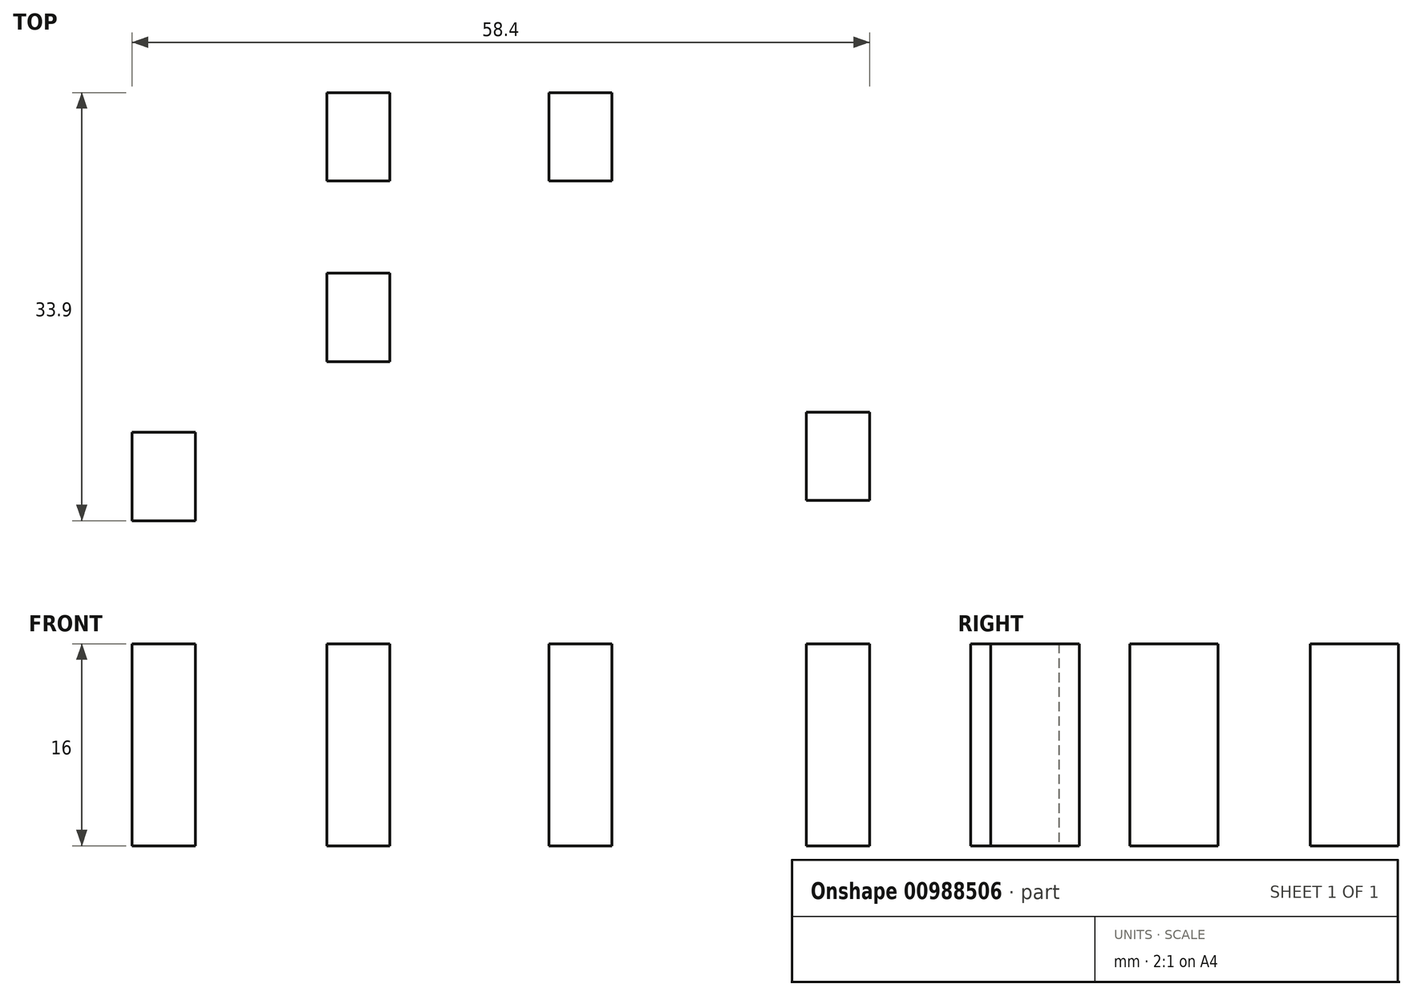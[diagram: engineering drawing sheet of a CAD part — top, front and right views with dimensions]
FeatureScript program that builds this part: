
annotation { "Feature Type Name" : "Feature", "Feature Type Description" : "" }
export const myFeature = defineFeature(function(context is Context, id is Id, definition is map)
    precondition{}
    {
        {
            var Q0;
            Q0=qCreatedBy(makeId("Top.planeOp"),FACE);
            var sketch = newSketch(context, id + "F0", { "sketchPlane" : qUnion([Q0])});
            skLineSegment(sketch, "E0.bottom", {"start": v(-19.73, 14.99) * mm, "end": v(-14.73, 14.99) * mm});
            skLineSegment(sketch, "E0.top", {"start": v(-19.73, 7.99) * mm, "end": v(-14.73, 7.99) * mm});
            skLineSegment(sketch, "E0.left", {"start": v(-19.73, 14.99) * mm, "end": v(-19.73, 7.99) * mm});
            skLineSegment(sketch, "E0.right", {"start": v(-14.73, 14.99) * mm, "end": v(-14.73, 7.99) * mm});
            skSolve(sketch);
        }
        {
            var Q0;
            Q0=makeQuery(id+"F0.imprint","IMPRINT",FACE,{"disambiguationData":[TD([[makeQuery(id+"F0.imprint","IMPRINT",EDGE,{"derivedFrom":sQuery(id+"F0.wireOp",EDGE,"E0.bottom")}),-1.0]])]});
            extrude(context, id + "F1", {"entities" : qUnion([Q0]), "endBound" : BoundingType.SYMMETRIC, "depth" : 16 * mm, "offsetDistance" : 25 * mm});
        }
        {
            var Q0;
            Q0=makeQuery(id+"F1.opExtrude","SWEPT_BODY",BODY,{"disambiguationData":[OSD([sQuery(id+"F0.wireOp",EDGE,"E0.bottom"),sQuery(id+"F0.wireOp",EDGE,"E0.top"),sQuery(id+"F0.wireOp",EDGE,"E0.left"),sQuery(id+"F0.wireOp",EDGE,"E0.right")])]});
            transform(context, id + "F2", {"entities" : qUnion([Q0]), "transformType" : TransformType.TRANSLATION_3D, "dx" : 17.6 * mm, "dy" : 0 * mm, "dz" : 0 * mm, "makeCopy" : true});
        }
        {
            var Q0;
            Q0=makeQuery(id+"F2.opPattern","COPY",BODY,{"derivedFrom":makeQuery(id+"F1.opExtrude","SWEPT_BODY",BODY,{"disambiguationData":[OSD([sQuery(id+"F0.wireOp",EDGE,"E0.bottom"),sQuery(id+"F0.wireOp",EDGE,"E0.top"),sQuery(id+"F0.wireOp",EDGE,"E0.left"),sQuery(id+"F0.wireOp",EDGE,"E0.right")])]}),"instanceName":"1"});
            transform(context, id + "F3", {"entities" : qUnion([Q0]), "transformType" : TransformType.TRANSLATION_3D, "dx" : 20.4 * mm, "dy" : -25.3 * mm, "dz" : 0 * mm, "makeCopy" : true});
        }
        {
            var Q0;
            Q0=makeQuery(id+"F1.opExtrude","SWEPT_BODY",BODY,{"disambiguationData":[OSD([sQuery(id+"F0.wireOp",EDGE,"E0.bottom"),sQuery(id+"F0.wireOp",EDGE,"E0.top"),sQuery(id+"F0.wireOp",EDGE,"E0.left"),sQuery(id+"F0.wireOp",EDGE,"E0.right")])]});
            transform(context, id + "F4", {"entities" : qUnion([Q0]), "transformType" : TransformType.TRANSLATION_3D, "dx" : -15.4 * mm, "dy" : -26.9 * mm, "dz" : 0 * mm, "makeCopy" : true});
        }
        {
            var Q0;
            Q0=makeQuery(id+"F1.opExtrude","SWEPT_BODY",BODY,{"disambiguationData":[OSD([sQuery(id+"F0.wireOp",EDGE,"E0.bottom"),sQuery(id+"F0.wireOp",EDGE,"E0.top"),sQuery(id+"F0.wireOp",EDGE,"E0.left"),sQuery(id+"F0.wireOp",EDGE,"E0.right")])]});
            transform(context, id + "F5", {"entities" : qUnion([Q0]), "transformType" : TransformType.TRANSLATION_3D, "dx" : 0 * mm, "dy" : -14.3 * mm, "dz" : 0 * mm, "makeCopy" : true});
        }
    });
